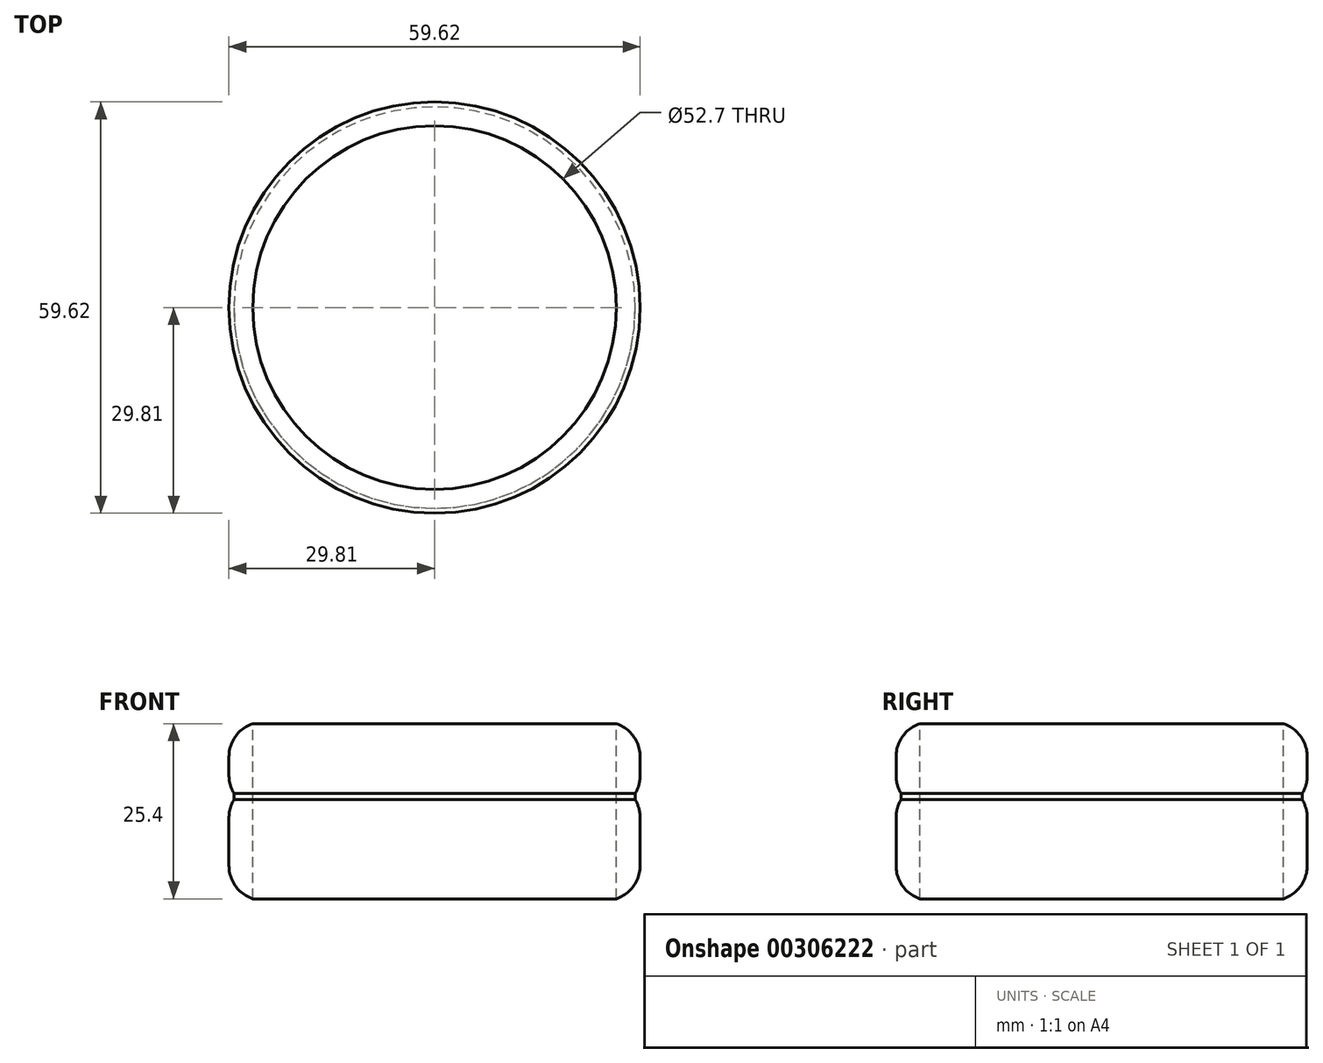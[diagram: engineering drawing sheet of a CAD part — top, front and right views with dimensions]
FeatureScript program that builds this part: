
annotation { "Feature Type Name" : "Feature", "Feature Type Description" : "" }
export const myFeature = defineFeature(function(context is Context, id is Id, definition is map)
    precondition{}
    {
        {
            var Q0;
            Q0=qCreatedBy(makeId("Top.planeOp"),FACE);
            var sketch = newSketch(context, id + "F0", { "sketchPlane" : qUnion([Q0])});
            skCircle(sketch, "E0", {"center": v(0, 0) * mm, "radius": 29.8 * mm});
            skSolve(sketch);
        }
        {
            var Q0;
            Q0 = qSketchRegion(id + "F0", true);
            extrude(context, id + "F1", {"entities" : qUnion([Q0]), "depth" : 25.4 * mm});
        }
        {
            var Q0;
            Q0=makeQuery(id+"F1.opExtrude","CAP_FACE",FACE,{"disambiguationData":[OSD([sQuery(id+"F0.wireOp",EDGE,"E0")])],"isStart":false});
            var sketch = newSketch(context, id + "F2", { "sketchPlane" : qUnion([Q0])});
            skCircle(sketch, "E1", {"center": v(0, 0) * mm, "radius": 26.35 * mm});
            skSolve(sketch);
        }
        {
            var Q0;
            Q0=makeQuery(id+"F2.imprint","IMPRINT",FACE,{"disambiguationData":[TD([[makeQuery(id+"F2.imprint","IMPRINT",EDGE,{"derivedFrom":sQuery(id+"F2.wireOp",EDGE,"E1")}),1.0]])]});
            extrude(context, id + "F3", {"entities" : qUnion([Q0]), "operationType" : NewBodyOperationType.REMOVE, "oppositeDirection" : true, "depth" : 25.4 * mm});
        }
        {
            var Q0;
            Q0=qCreatedBy(makeId("Right.planeOp"),FACE);
            var sketch = newSketch(context, id + "F4", { "sketchPlane" : qUnion([Q0])});
            skLineSegment(sketch, "E2.bottom", {"start": v(-31.98, 15.29) * mm, "end": v(-29.1, 15.29) * mm});
            skLineSegment(sketch, "E2.top", {"start": v(-31.98, 14.37) * mm, "end": v(-29.1, 14.37) * mm});
            skLineSegment(sketch, "E2.left", {"start": v(-31.98, 15.29) * mm, "end": v(-31.98, 14.37) * mm});
            skLineSegment(sketch, "E2.right", {"start": v(-29.1, 15.29) * mm, "end": v(-29.1, 14.37) * mm});
            skSolve(sketch);
        }
        {
            var Q0;
            Q0=qCreatedBy(makeId("Right.planeOp"),FACE);
            var sketch = newSketch(context, id + "F5", { "sketchPlane" : qUnion([Q0])});
            skLineSegment(sketch, "E3", {"start": v(0, 0) * mm, "end": v(0, 63.78) * mm, "construction": true});
            skSolve(sketch);
        }
        {
            var Q0;
            Q0 = qSketchRegion(id + "F4", true);
            var Q1;
            Q1=sQuery(id+"F5.wireOp",EDGE,"E3");
            revolve(context, id + "F6", {"operationType" : NewBodyOperationType.REMOVE, "entities" : qUnion([Q0]), "axis" : qUnion([Q1]), "revolveType" : RevolveType.FULL, "oppositeDirection" : true});
        }
        {
            var Q0;
            {var subQ0=sQuery(id+"F0.wireOp",EDGE,"E0");Q0=makeQuery(id+"F6.boolean.opBoolean","SPLIT",FACE,{"disambiguationData":[TD([makeQuery(id+"F1.opExtrude","CAP_FACE",FACE,{"disambiguationData":[OSD([subQ0])],"isStart":false})])],"derivedFrom":makeQuery(id+"F1.opExtrude","SWEPT_FACE",FACE,{"disambiguationData":[OSD([subQ0])]})});}
            var Q1;
            {var subQ0=sQuery(id+"F0.wireOp",EDGE,"E0");Q1=makeQuery(id+"F6.boolean.opBoolean","SPLIT",FACE,{"disambiguationData":[TD([makeQuery(id+"F1.opExtrude","CAP_FACE",FACE,{"disambiguationData":[OSD([subQ0])],"isStart":true})])],"derivedFrom":makeQuery(id+"F1.opExtrude","SWEPT_FACE",FACE,{"disambiguationData":[OSD([subQ0])]})});}
            fillet(context, id + "F7", {"entities" : qUnion([Q0, Q1]), "radius" : 5.08 * mm, "tangentPropagation" : true, "allowEdgeOverflow" : false});
        }
    });
